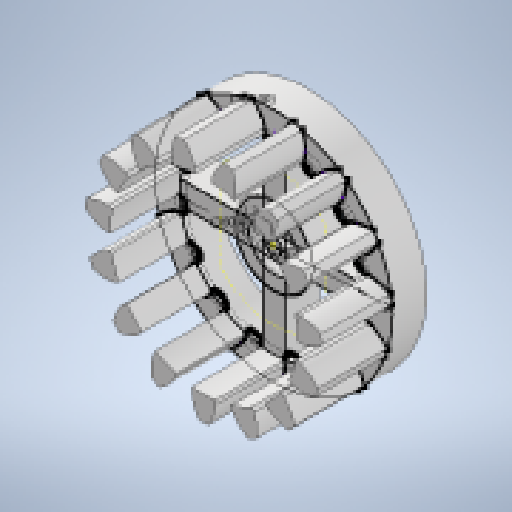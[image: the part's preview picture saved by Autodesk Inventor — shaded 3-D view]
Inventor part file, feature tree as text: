
AUTODESK INVENTOR PART (.ipt)
format: ipt  version: 2023 (Build 270158000, 158)  size: 694,784 bytes
history: native  units: mm
features: extrude x3, other x3, plane x1, reference x1
ambient origin geometry x8: Origin, YZ Plane, XZ Plane, XY Plane, X Axis, Y Axis, Z Axis, Center Point
bodies: Body1 (feature_tree)
feature tree (8):
  extrude  "Extrusion2"  Depth=2.3mm
  extrude  "Extrusion3"  Depth=27.0mm
  plane  "Work Plane1"
  extrude  "Extrusion4"  Depth=0.5mm
  reference  "Reference1"
  parser-record x1  (decoder bookkeeping rows leaked as tree rows — omitted from the tree; the rows remain in map.json)
  other  "Assembly_V7.iam"
  other  "motor:2"
note: 1 file-system path scrubbed to <path> (originals preserved in map.json)
